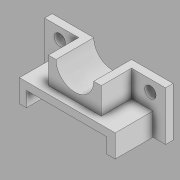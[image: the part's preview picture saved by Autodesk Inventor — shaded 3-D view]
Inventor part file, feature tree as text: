
AUTODESK INVENTOR PART (.ipt)
format: ipt  version: 2020 (Build 240168000, 168)  size: 152,064 bytes
history: native  units: in
note: dims shown in document units (in); Inventor stores cm internally (conversion verified against a paired STEP export)
features: extrude x7, sketch x7, other x1
ambient origin geometry x8: Origin, YZ Plane, XZ Plane, XY Plane, X Axis, Y Axis, Z Axis, Center Point
bodies: Body1 (feature_tree)
feature tree (15):
  other  "Sólido1"
  extrude  "Bloque_Posterior"  Depth=2.4375in
  extrude  "Bloque_Inferior"  Depth=4.75in
  extrude  "Bloque_Superior"  Depth=1.125in
  extrude  "Orificio_Inferior"  Depth=2.625in
  extrude  "Agujero_Central"  Depth=1.3125in
  extrude  "Agujero_Izquierdo"  Depth=4.0in
  extrude  "Agujero_Derecho"  Depth=1.875in TaperAngle=0.0deg
  sketch  "Boceto1"  dims[d0=6.0in d1=2.4375in]
  sketch  "Boceto2"  dims[d2=0.375in d3=0.0in d4=4.75in]
  sketch  "Boceto3"  dims[d5=1.125in d6=2.375in]
  sketch  "Boceto4"  dims[d7=1.875in d8=0.0in d9=2.625in]
  sketch  "Boceto5"  dims[d10=1.3125in d11=1.3125in]
  sketch  "Boceto6"  dims[d12=1.5in d13=0.0in d14=4.0in]
  sketch  "Boceto7"  dims[d15=0.75in d16=1.875in d17=0.0in d18=0.938in d19=0.0in d20=1.875in d21=1.875in d22=0.0in d23=0.5625in d24=0.75in d25=0.5625in d26=0.375in d27=0.0in d28=0.75in d29=0.5625in d30=0.5625in d31=0.375in d32=0.0in]
